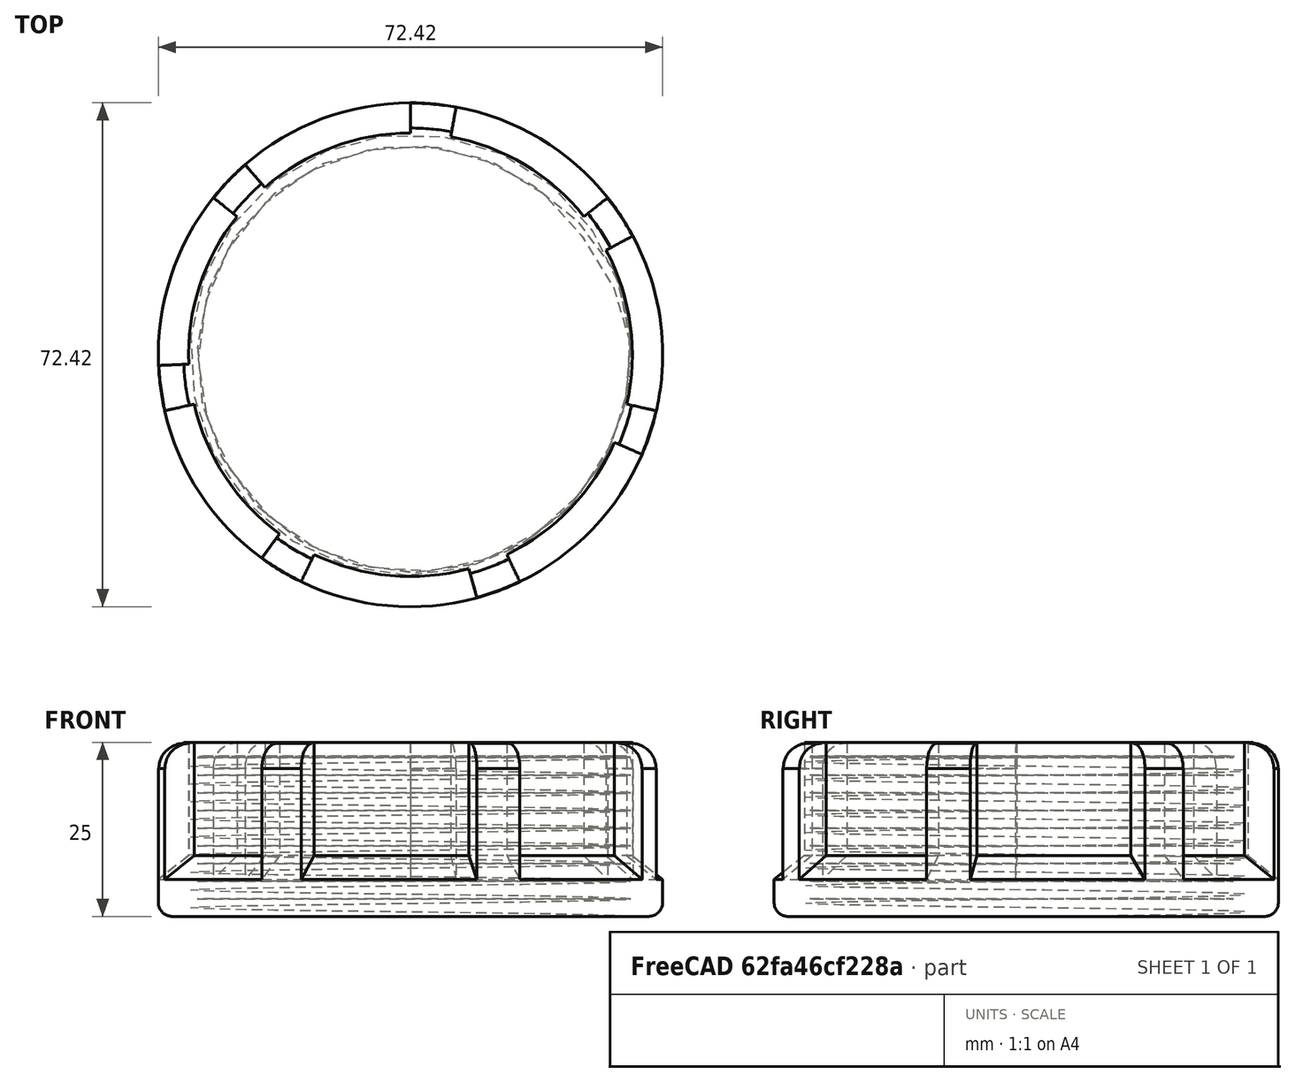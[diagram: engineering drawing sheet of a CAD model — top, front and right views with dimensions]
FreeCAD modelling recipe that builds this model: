
FCSTD DOCUMENT  (FreeCAD 0.21R33771 (Git))
Label: krishka3
License: All rights reserved
LicenseURL: http://en.wikipedia.org/wiki/All_rights_reserved
objects: Sketcher::SketchObject×3, PartDesign::Groove×2, PartDesign::Body×2, PartDesign::Pad×1, PartDesign::PolarPattern×1, Part::Part2DObjectPython×1, Part::Helix×1, PartDesign::AdditivePipe×1, Part::Cut×1, Part::Fillet×1
note: 18 computed .brp shape members not serialized (recipe doc carries the construction recipe); baked Part::Feature solids carry a one-line shape summary decoded from their .brp

FEATURE [Sketcher::SketchObject] Sketch
  FullyConstrained = false
  MapMode = 5
  Support = -> [XY_Plane001]
  sketch-geometry (1):
    g0: Circle CenterX=0 CenterY=0 CenterZ=0 NormalX=0 NormalY=0 NormalZ=1 AngleXU=0 Radius=36.2112
  constraints (1):
    c: Coincident(g0,g-1)
FEATURE [PartDesign::Pad] Pad
  Direction = (0,0,1)
  Length = 25
  Length2 = 10
  Profile = -> Sketch
  ReferenceAxis = -> Sketch [N_Axis]
  Refine = true
  Type = 0
FEATURE [Sketcher::SketchObject] Sketch001
  FullyConstrained = false
  MapMode = 5
  Placement = pos=(0,0,0) rot=(0.57735,0.57735,0.57735;2.0944rad)
  Support = -> [YZ_Plane001]
  sketch-geometry (5):
    g0: LineSegment StartX=31.8636 StartY=27.8702 StartZ=0 EndX=31.8636 EndY=8.73544 EndZ=0
    g1: LineSegment StartX=31.8636 StartY=8.73544 StartZ=0 EndX=37.3544 EndY=4.40932 EndZ=0
    g2: LineSegment StartX=31.8636 StartY=27.8702 StartZ=0 EndX=40.0166 EndY=27.8702 EndZ=0
    g3: LineSegment StartX=40.0166 StartY=27.8702 StartZ=0 EndX=40.0166 EndY=4.40932 EndZ=0
    g4: LineSegment StartX=40.0166 StartY=4.40932 StartZ=0 EndX=37.3544 EndY=4.40932 EndZ=0
  constraints (7):
    c: Coincident(g1,g0)
    c: Coincident(g2,g0)
    c: Horizontal(g2)
    c: Vertical(g3)
    c: Coincident(g4,g1)
    c: Horizontal(g4)
    c: Vertical(g0)
FEATURE [PartDesign::Groove] Groove
  Angle = 41
  Axis = (-2e-16,3e-16,1)
  Base = (0,0,0)
  BaseFeature = -> Pad
  Profile = -> Sketch001
  ReferenceAxis = -> Sketch001 [V_Axis]
  Refine = true
FEATURE [PartDesign::PolarPattern] PolarPattern
  Angle = 360
  Axis = -> Z_Axis001
  BaseFeature = -> Groove
  Occurrences = 7
  Originals = -> [Groove]
  Refine = true
FEATURE [Sketcher::SketchObject] Sketch002
  FullyConstrained = false
  MapMode = 5
  Placement = pos=(0,0,0) rot=(0.57735,0.57735,0.57735;2.0944rad)
  Support = -> [YZ_Plane001]
  sketch-geometry (5):
    g0: ArcOfCircle CenterX=32.564 CenterY=21.2627 CenterZ=0 NormalX=0 NormalY=0 NormalZ=1 AngleXU=0 Radius=3.59386 StartAngle=0 EndAngle=1.56596
    g1: LineSegment StartX=32.5814 StartY=24.8565 StartZ=0 EndX=32.5814 EndY=28.0465 EndZ=0
    g2: LineSegment StartX=32.5814 StartY=28.0465 StartZ=0 EndX=43.0826 EndY=28.0465 EndZ=0
    g3: LineSegment StartX=43.0826 StartY=28.0465 StartZ=0 EndX=43.0826 EndY=21.2627 EndZ=0
    g4: LineSegment StartX=43.0826 StartY=21.2627 StartZ=0 EndX=36.1579 EndY=21.2627 EndZ=0
  constraints (10):
    c: Horizontal(g2)
    c: Coincident(g3,g2)
    c: Vertical(g3)
    c: Vertical(g1)
    c: DistanceY(g1,g1) = 3.19
    c: Coincident(g2,g1)
    c: Coincident(g4,g3)
    c: Horizontal(g4)
    c: Coincident(g0,g1)
    c: Coincident(g4,g0)
FEATURE [PartDesign::Groove] Groove001
  Angle = 360
  Axis = (-2e-16,3e-16,1)
  Base = (0,0,0)
  BaseFeature = -> PolarPattern
  Profile = -> Sketch002
  ReferenceAxis = -> Sketch002 [V_Axis]
  Refine = true
FEATURE [PartDesign::Body] Body001
  Group = -> [Sketch,Pad,Sketch001,Groove,PolarPattern,Sketch002,Groove001]
  Origin = -> Origin001
  Tip = -> Groove001
FEATURE [Part::Part2DObjectPython] BThreadProfile  # Draft 2D object (typed FeaturePython)
  Area = 2977.93
  Closed = true
  Continuity = C2
  Height = 23
  Helix = Helix
  Instructions = Expand this with the ... button to view instructions | Sweep this object along a helix of the same pitch to produce your thread. | It is recommended to make the helix in the ThreadProfile workbench. | If there is an active Body the ThreadProfile object will be put into it.,If not it can be dragged and dropped into the body later. | If there is an active Body when the helix is made there will be made a ShapeBinder for it | For internal threads you will need to cut the Sweep object out of a cylinder, or if using Part Design sweep it as a Subtractive Pipe. | Always use Frenet mode | I have provided some presets, but it is possible there could be some errors.  Double check for mission critical applications. | Also, the tolerances might be different from what you wish to have.  I believe the internal minor diameters are all minimum and the external are all maximum.
  InternalOrExternal = 1
  MakeFace = true
  MinorDiameter = 60
  Parameterization = 1
  Pitch = 2.54
  Points = (120) [(31.611,1.65897,0),(31.3091,3.29533,0),(30.9231,4.90467,0),(30.455,6.48268,0),(29.9069,8.0252,0),(29.2813,9.52821,0),(28.5808,10.9878,0),+113 more]
  Presets = 0
  Quality = 6
  ThreadCount = 9.05512
  Variants = 0
  Version = 1.89
  external2S_data = [-0.00461051,-0.00886426,-0.0128148,-0.0165028,-0.0199596,-0.0232105,-0.0262759,-0.0291725,-0.0319145,-0.0345137,-0.0369805,-0.0393235,-0.0415505,-0.0436681,-0.0456823,-0.0475981,-0.0494204,-0.0511532,-0.0528003,-0.0543649,-0.0558502,+698 more]
  external3S_data = [-0.00677828,-0.0128149,-0.0182584,-0.0232106,-0.0277444,-0.0319145,-0.0357632,-0.0393236,-0.0426227,-0.0456823,-0.0485208,-0.0511533,-0.0535928,-0.0558503,-0.0579353,-0.059856,-0.0616195,-0.0632319,-0.0646984,-0.0660239,-0.0672123,+698 more]
  external45_data = [-0.00137363,-0.00271738,-0.00403219,-0.00531893,-0.00657844,-0.00781148,-0.00901878,-0.010201,-0.0113589,-0.012493,-0.0136039,-0.0146921,-0.0157583,-0.0168028,-0.0178261,-0.0188288,-0.0198112,-0.0207738,-0.0217169,-0.0226409,-0.0235462,+698 more]
  external_data = [0.651362,0.640051,0.628739,0.617428,0.606116,0.594804,0.583493,0.572181,0.56087,0.549558,0.538246,0.526935,0.515623,0.504312,0.493,0.481688,0.470377,0.459065,0.447754,0.436442,0.42513,0.413819,0.402507,0.391196,0.379884,0.368572,0.357261,+692 more]
  internal2S_data = [0,0,0,0,0,0,0,0,0,0,0,0,0,0,0,0,0,0,0,0,0,0,0,0,0,0,0,0,0,0,0,0,0,0,0,0,0,0,0,0,0,0,0,0,0,0,0,0,0,0,0,0,0,0,0,0,0,0,0,0,0,0,0,0,0,0,0,0,0,0,0,0,0,0,0,0,0,0,0,0,0,0,0,0,0,0,0,0,0,0,0.00481128,0.00962256,0.0144338,0.0192451,0.0240564,+624 more]
  internal3S_data = [0,0,0,0,0,0,0,0,0,0,0,0,0,0,0,0,0,0,0,0,0,0,0,0,0,0,0,0,0,0,0,0,0,0,0,0,0,0,0,0,0,0,0,0,0,0,0,0,0,0,0,0,0,0,0,0,0,0,0,0,0.00721688,0.0144338,0.0216506,0.0288675,0.0360844,0.0433013,0.0505181,0.057735,0.0649519,0.0721688,0.0793857,0.0866025,+647 more]
  internal45_data = [0,0,0,0,0,0,0,0,0,0,0,0,0,0,0,0,0,0,0,0,0,0,0,0,0,0,0,0,0,0,0,0,0,0,0,0,0,0,0,0,0,0,0,0,0,0,0,0,0,0,0,0,0,0,0,0,0,0,0,0,0,0,0,0,0,0,0,0,0,0,0,0,0,0,0,0,0,0,0,0,0,0,0,0,0,0,0,0,0,0,0,0,0,0,0,0,0,0,0,0,0,0,0,0,0,0,0,0,0,0,0,0,0,0,0,0,0,0,0,0,+599 more]
  internal_data = [0.6514,0.640089,0.628777,0.617466,0.606154,0.594842,0.583531,0.572219,0.560908,0.549596,0.538284,0.526973,0.515661,0.50435,0.493038,0.481727,0.470415,0.459103,0.447792,0.43648,0.425169,0.413857,0.402545,0.391234,0.379922,0.368611,0.357299,+692 more]
  preset_names = Buttress presets | 1/2-12 | 1/2-16 | 1/2-20 | 5/8-12 | 5/8-16 | 5/8-20 | 3/4-12 | 3/4-16 | 3/4-20 | 7/8-10 | 7/8-12 | 7/8-16 | 1-10 | 1-12 | 1-16 | 1 1/4-8 | 1 1/4-10 | 1 1/4-12 | 1 3/8-8 | 1 3/8-10 | 1 3/8-12 | 1 1/2-8 | 1 1/2-10 | 1 1/2-12 | 1 3/4-6 | 1 3/4-6 | 1 3/4-10 | 2-6 | 2-8 | 2-10 | 2 1/4-6 | 2 1/4-8 | 2 1/4-10 | 2 1/2-6 | 2 1/2-8 | 2 1/2-10 | 2 3/4-5 | 2 3/4-6 | 2 3/4-8 | 3-5 | 3-6 | 3-8 | 3 1/2-5 | 3 1/2-6 | 3 1/2-8 | 4-5 | 4-6 | 4-8 | 4 1/2-4 | 4 1/2-5 | 4 1/2-6 | 5-4 | 5-5 | 5-6 | 5 1/2-4 | 5 1/2-5 | 5 1/2-6 | 6-4 | 6-5 | 6-6 | 7-3 | 7-4 | 7-5 | 8-3 | 8-4 | 8-5 | 9-3 | 9-4 | 9-5 | 10-3 | 10-4 | 10-5 | 11-2.5 | 11-3 | 11-4 | 12-2.5 | 12-3 | 12-4 | 13-2.5 | 13-3 | 13-4 | 14-2.5 | 14-3 | 14-4 | 16-2.5 | 16-3 | 16-4 | 18-2 | 18-2.5 | 18-3 | 20-2 | 20-2.5 | 20-3 | 22-2 | 22-2.5 | 22-3 | 24-2 | 24-2.5 | 24-3
  presets_data = [0,0,0,2.11667,11.2674,11.3271,1.5875,11.6214,11.6745,1.27,11.8342,11.8826,2.11667,14.442,14.5025,1.5875,14.7961,14.8498,1.27,15.0088,15.0579,2.11667,17.6167,17.6778,1.5875,17.9708,18.0251,1.27,18.1835,18.2332,2.54,20.5085,20.575,2.11667,+266 more]
FEATURE [Part::Helix] Helix
  Angle = 0
  AttacherType = Attacher::AttachEngine3D
  Height = 23
  LocalCoord = 0
  Pitch = 2.54
  Radius = 1
  SegmentLength = 1
  Style = 0
  expr: AttachmentOffset = BThreadProfile.AttachmentOffset
  expr: Height = BThreadProfile.ThreadCount * BThreadProfile.Pitch
  expr: MapMode = BThreadProfile.MapMode
  expr: MapPathParameter = BThreadProfile.MapPathParameter
  expr: MapReversed = BThreadProfile.MapReversed
  expr: Pitch = BThreadProfile.Pitch
  expr: SegmentLength = 1
  expr: Support = BThreadProfile.Support
FEATURE [PartDesign::AdditivePipe] AdditivePipe
  AuxilleryCurvelinear = true
  AuxillerySpineTangent = false
  Binormal = (0,0,0)
  Mode = 2
  Profile = -> BThreadProfile
  Refine = true
  Spine = -> Helix [Edge1,Edge2,Edge3,Edge4,Edge5,Edge6,Edge7,Edge8,Edge9,Edge10]
  SpineTangent = false
  Transformation = 0
  Transition = 0
FEATURE [PartDesign::Body] Body
  Group = -> [BThreadProfile,Helix,AdditivePipe]
  Origin = -> Origin
  Tip = -> AdditivePipe
FEATURE [Part::Cut] Cut
  Base = -> Body001
  Refine = true
  Tool = -> Body
FEATURE [Part::Fillet] Fillet
  Base = -> Cut
  Edges = 1 edges r=2: [Edge1]
